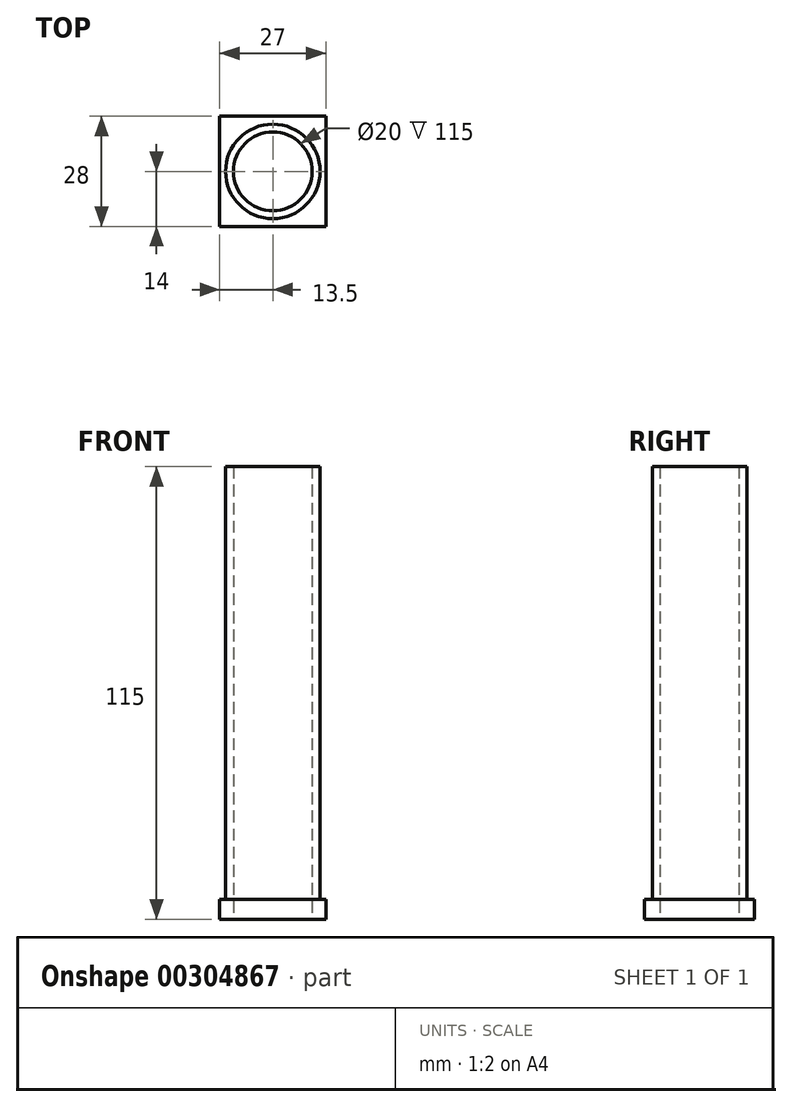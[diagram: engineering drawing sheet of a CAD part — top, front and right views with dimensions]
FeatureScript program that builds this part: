
annotation { "Feature Type Name" : "Feature", "Feature Type Description" : "" }
export const myFeature = defineFeature(function(context is Context, id is Id, definition is map)
    precondition{}
    {
        {
            var Q0;
            Q0=qCreatedBy(makeId("Top.planeOp"),FACE);
            var sketch = newSketch(context, id + "F0", { "sketchPlane" : qUnion([Q0])});
            skLineSegment(sketch, "E0.bottom", {"start": v(13.5, -14) * mm, "end": v(-13.5, -14) * mm});
            skLineSegment(sketch, "E0.top", {"start": v(13.5, 14) * mm, "end": v(-13.5, 14) * mm});
            skLineSegment(sketch, "E0.left", {"start": v(13.5, -14) * mm, "end": v(13.5, 14) * mm});
            skLineSegment(sketch, "E0.right", {"start": v(-13.5, -14) * mm, "end": v(-13.5, 14) * mm});
            skPoint(sketch, "E0.middle", {"position": v(0, 0) * mm});
            skSolve(sketch);
        }
        {
            var Q0;
            Q0 = qSketchRegion(id + "F0", true);
            extrude(context, id + "F1", {"entities" : qUnion([Q0]), "depth" : 5 * mm});
        }
        {
            var Q0;
            Q0=makeQuery(id+"F1.opExtrude","CAP_FACE",FACE,{"disambiguationData":[OSD([sQuery(id+"F0.wireOp",EDGE,"E0.bottom"),sQuery(id+"F0.wireOp",EDGE,"E0.top"),sQuery(id+"F0.wireOp",EDGE,"E0.left"),sQuery(id+"F0.wireOp",EDGE,"E0.right")])],"isStart":false});
            var sketch = newSketch(context, id + "F2", { "sketchPlane" : qUnion([Q0])});
            skCircle(sketch, "E1", {"center": v(0, 0) * mm, "radius": 12 * mm});
            skCircle(sketch, "E2", {"center": v(0, 0) * mm, "radius": 10 * mm});
            skSolve(sketch);
        }
        {
            var Q0;
            Q0 = qSketchRegion(id + "F2", true);
            extrude(context, id + "F3", {"entities" : qUnion([Q0]), "operationType" : NewBodyOperationType.ADD, "depth" : 110 * mm});
        }
        {
            var Q0;
            Q0=makeQuery(id+"F3.boolean.opBoolean","SPLIT",FACE,{"disambiguationData":[TD([makeQuery(id+"F3.opExtrude","SWEPT_FACE",FACE,{"disambiguationData":[OSD([sQuery(id+"F2.wireOp",EDGE,"E2")])]})])],"derivedFrom":makeQuery(id+"F1.opExtrude","CAP_FACE",FACE,{"disambiguationData":[OSD([sQuery(id+"F0.wireOp",EDGE,"E0.bottom"),sQuery(id+"F0.wireOp",EDGE,"E0.top"),sQuery(id+"F0.wireOp",EDGE,"E0.left"),sQuery(id+"F0.wireOp",EDGE,"E0.right")])],"isStart":false})});
            var Q1;
            Q1=makeQuery(id+"F1.opExtrude","CAP_FACE",FACE,{"disambiguationData":[OSD([sQuery(id+"F0.wireOp",EDGE,"E0.bottom"),sQuery(id+"F0.wireOp",EDGE,"E0.top"),sQuery(id+"F0.wireOp",EDGE,"E0.left"),sQuery(id+"F0.wireOp",EDGE,"E0.right")])],"isStart":true});
            extrude(context, id + "F4", {"entities" : qUnion([Q0]), "operationType" : NewBodyOperationType.REMOVE, "endBound" : BoundingType.UP_TO_SURFACE, "oppositeDirection" : true, "endBoundEntityFace" : qUnion([Q1]), "depth" : 25 * mm});
        }
    });
